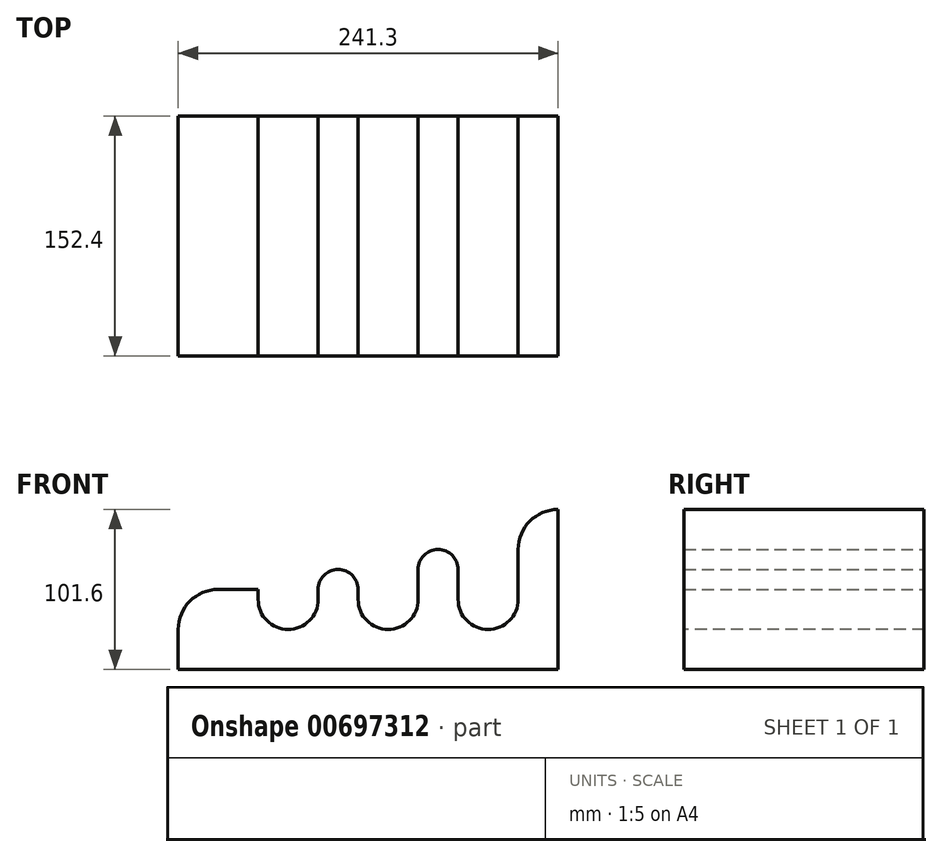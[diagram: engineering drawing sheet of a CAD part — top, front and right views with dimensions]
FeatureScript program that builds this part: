
annotation { "Feature Type Name" : "Feature", "Feature Type Description" : "" }
export const myFeature = defineFeature(function(context is Context, id is Id, definition is map)
    precondition{}
    {
        {
            var Q0;
            Q0=qCreatedBy(makeId("Front.planeOp"),FACE);
            var sketch = newSketch(context, id + "F0", { "sketchPlane" : qUnion([Q0])});
            skLineSegment(sketch, "E0.bottom", {"start": v(-172.92, 215.9) * mm, "end": v(-147.52, 215.9) * mm});
            skLineSegment(sketch, "E0.top", {"start": v(-172.92, 0) * mm, "end": v(-147.52, 0) * mm});
            skLineSegment(sketch, "E0.left", {"start": v(-172.92, 190.5) * mm, "end": v(-172.92, 152.4) * mm});
            skLineSegment(sketch, "E0.right", {"start": v(-147.52, 215.9) * mm, "end": v(-147.52, 0) * mm});
            skLineSegment(sketch, "E1.bottom", {"start": v(-147.52, 215.9) * mm, "end": v(-249.12, 215.9) * mm});
            skLineSegment(sketch, "E1.top", {"start": v(-172.92, 190.5) * mm, "end": v(-249.12, 190.5) * mm});
            skLineSegment(sketch, "E1.left", {"start": v(-147.52, 215.9) * mm, "end": v(-147.52, 190.5) * mm});
            skLineSegment(sketch, "E1.right", {"start": v(-249.12, 215.9) * mm, "end": v(-249.12, 190.5) * mm});
            skLineSegment(sketch, "E2.bottom", {"start": v(-172.92, 152.4) * mm, "end": v(-223.72, 152.4) * mm});
            skLineSegment(sketch, "E2.top", {"start": v(-172.92, 127) * mm, "end": v(-223.72, 127) * mm});
            skLineSegment(sketch, "E2.left", {"start": v(-147.52, 152.4) * mm, "end": v(-147.52, 127) * mm});
            skLineSegment(sketch, "E2.right", {"start": v(-223.72, 152.4) * mm, "end": v(-223.72, 127) * mm});
            skLineSegment(sketch, "E3.bottom", {"start": v(-172.92, 88.9) * mm, "end": v(-211.02, 88.9) * mm});
            skLineSegment(sketch, "E3.top", {"start": v(-172.92, 63.5) * mm, "end": v(-211.02, 63.5) * mm});
            skLineSegment(sketch, "E3.left", {"start": v(-147.52, 88.9) * mm, "end": v(-147.52, 63.5) * mm});
            skLineSegment(sketch, "E3.right", {"start": v(-211.02, 88.9) * mm, "end": v(-211.02, 63.5) * mm});
            skLineSegment(sketch, "E4.trimOffspring", {"start": v(-172.92, 63.5) * mm, "end": v(-172.92, 0) * mm});
            skLineSegment(sketch, "E5.trimOffspring", {"start": v(-172.92, 127) * mm, "end": v(-172.92, 88.9) * mm});
            skLineSegment(sketch, "E6.left", {"start": v(-172.92, 0) * mm, "end": v(-172.92, 25.4) * mm});
            skLineSegment(sketch, "E7.bottom", {"start": v(-172.92, 0) * mm, "end": v(-198.32, 0) * mm});
            skLineSegment(sketch, "E7.top", {"start": v(-172.92, 25.4) * mm, "end": v(-198.32, 25.4) * mm});
            skLineSegment(sketch, "E7.right", {"start": v(-198.32, 0) * mm, "end": v(-198.32, 25.4) * mm});
            skPoint(sketch, "E8.oppositeSnap0", {"position": v(-160.22, 0) * mm});
            skLineSegment(sketch, "E8.bottom", {"start": v(-147.52, 0) * mm, "end": v(-160.22, 0) * mm});
            skLineSegment(sketch, "E8.top", {"start": v(-147.52, -25.4) * mm, "end": v(-160.22, -25.4) * mm});
            skLineSegment(sketch, "E8.left", {"start": v(-147.52, 0) * mm, "end": v(-147.52, -25.4) * mm});
            skLineSegment(sketch, "E8.right", {"start": v(-160.22, 0) * mm, "end": v(-160.22, -25.4) * mm});
            skSolve(sketch);
        }
        {
            var Q0;
            Q0=qSketchRegion(id+"F0",true);
            extrude(context, id + "F1", {"entities" : qUnion([Q0]), "depth" : 152.4 * mm, "offsetDistance" : 25.4 * mm});
        }
        {
            var Q0;
            Q0=makeQuery(id+"F1.opExtrude","SWEPT_FACE",FACE,{"disambiguationData":[OSD([sQuery(id+"F0.wireOp",EDGE,"E8.right")])]});
            var sketch = newSketch(context, id + "F2", { "sketchPlane" : qUnion([Q0])});
            skLineSegment(sketch, "E9.bottom", {"start": v(0, 0) * mm, "end": v(152.4, 0) * mm});
            skLineSegment(sketch, "E9.top", {"start": v(0, -25.4) * mm, "end": v(152.4, -25.4) * mm});
            skLineSegment(sketch, "E9.left", {"start": v(0, 0) * mm, "end": v(0, -25.4) * mm});
            skLineSegment(sketch, "E9.right", {"start": v(152.4, 0) * mm, "end": v(152.4, -25.4) * mm});
            skSolve(sketch);
        }
        {
            var Q0;
            Q0=qSketchRegion(id+"F2",true);
            extrude(context, id + "F3", {"entities" : qUnion([Q0]), "operationType" : NewBodyOperationType.ADD, "depth" : 38.1 * mm, "offsetDistance" : 25.4 * mm});
        }
        {
            var Q0;
            Q0=makeQuery(id+"F3.opExtrude","CAP_EDGE",EDGE,{"disambiguationData":[OSD([sQuery(id+"F2.wireOp",EDGE,"E9.top")])],"isStart":false});
            fillet(context, id + "F4", {"entities" : qUnion([Q0]), "radius" : 25.4 * mm, "tangentPropagation" : true, "allowEdgeOverflow" : false});
        }
        {
            var Q0;
            Q0=makeQuery(id+"F3.boolean.opBoolean","MERGE",FACE,{"derivedFrom":[makeQuery(id+"F1.opExtrude","CAP_FACE",FACE,{"disambiguationData":[OSD([sQuery(id+"F0.wireOp",EDGE,"E0.top"),sQuery(id+"F0.wireOp",EDGE,"E0.left"),sQuery(id+"F0.wireOp",EDGE,"E0.right"),sQuery(id+"F0.wireOp",EDGE,"E1.bottom"),sQuery(id+"F0.wireOp",EDGE,"E1.top"),sQuery(id+"F0.wireOp",EDGE,"E1.left"),sQuery(id+"F0.wireOp",EDGE,"E1.right"),sQuery(id+"F0.wireOp",EDGE,"E2.bottom"),sQuery(id+"F0.wireOp",EDGE,"E2.top"),sQuery(id+"F0.wireOp",EDGE,"E2.left"),sQuery(id+"F0.wireOp",EDGE,"E2.right"),sQuery(id+"F0.wireOp",EDGE,"E3.bottom"),sQuery(id+"F0.wireOp",EDGE,"E3.top"),sQuery(id+"F0.wireOp",EDGE,"E3.left"),sQuery(id+"F0.wireOp",EDGE,"E3.right"),sQuery(id+"F0.wireOp",EDGE,"E4.trimOffspring"),sQuery(id+"F0.wireOp",EDGE,"E5.trimOffspring"),sQuery(id+"F0.wireOp",EDGE,"E7.bottom"),sQuery(id+"F0.wireOp",EDGE,"E7.top"),sQuery(id+"F0.wireOp",EDGE,"E7.right"),sQuery(id+"F0.wireOp",EDGE,"E8.top"),sQuery(id+"F0.wireOp",EDGE,"E8.left"),sQuery(id+"F0.wireOp",EDGE,"E8.right")])],"isStart":false}),makeQuery(id+"F3.opExtrude","SWEPT_FACE",FACE,{"disambiguationData":[OSD([sQuery(id+"F2.wireOp",EDGE,"E9.right")])]})]});
            var sketch = newSketch(context, id + "F5", { "sketchPlane" : qUnion([Q0])});
            skLineSegment(sketch, "E10.bottom", {"start": v(-249.12, 215.9) * mm, "end": v(-147.52, 215.9) * mm});
            skLineSegment(sketch, "E10.top", {"start": v(-211.02, 254) * mm, "end": v(-147.52, 254) * mm});
            skLineSegment(sketch, "E10.left", {"start": v(-249.12, 215.9) * mm, "end": v(-249.12, 215.9) * mm});
            skLineSegment(sketch, "E10.right", {"start": v(-147.52, 215.9) * mm, "end": v(-147.52, 254) * mm});
            skPoint(sketch, "E11.visualSharp", {"position": v(-249.12, 254) * mm});
            skArc(sketch, "E11.filletArc", {"start": v(-211.02, 254) * mm, "mid": v(-237.96, 242.84) * mm, "end": v(-249.12, 215.9) * mm});
            skSolve(sketch);
        }
        {
            var Q0;
            Q0=makeQuery(id+"F5.imprint","IMPRINT",FACE,{"disambiguationData":[TD([[makeQuery(id+"F5.imprint","IMPRINT",EDGE,{"derivedFrom":sQuery(id+"F5.wireOp",EDGE,"E10.bottom")}),-1.0]])]});
            extrude(context, id + "F6", {"entities" : qUnion([Q0]), "operationType" : NewBodyOperationType.ADD, "oppositeDirection" : true, "depth" : 151.9 * mm, "offsetDistance" : 25.4 * mm});
        }
        {
            var Q0;
            Q0=makeQuery(id+"F1.opExtrude","SWEPT_EDGE",EDGE,{"disambiguationData":[OSD([sQuery(id+"F0.wireOp",EDGE,"E3.bottom"),sQuery(id+"F0.wireOp",EDGE,"E5.trimOffspring")])]});
            fillet(context, id + "F7", {"entities" : qUnion([Q0]), "radius" : 19.05 * mm, "tangentPropagation" : true, "allowEdgeOverflow" : false});
        }
        {
            var Q0;
            Q0=makeQuery(id+"F1.opExtrude","SWEPT_EDGE",EDGE,{"disambiguationData":[OSD([sQuery(id+"F0.wireOp",EDGE,"E0.left"),sQuery(id+"F0.wireOp",EDGE,"E1.top")])]});
            var Q1;
            Q1=makeQuery(id+"F1.opExtrude","SWEPT_EDGE",EDGE,{"disambiguationData":[OSD([sQuery(id+"F0.wireOp",EDGE,"E2.top"),sQuery(id+"F0.wireOp",EDGE,"E5.trimOffspring")])]});
            fillet(context, id + "F8", {"entities" : qUnion([Q0, Q1]), "radius" : 19.05 * mm, "tangentPropagation" : true, "allowEdgeOverflow" : false});
        }
        {
            var Q0;
            Q0=makeQuery(id+"F1.opExtrude","SWEPT_EDGE",EDGE,{"disambiguationData":[OSD([sQuery(id+"F0.wireOp",EDGE,"E0.left"),sQuery(id+"F0.wireOp",EDGE,"E2.bottom")])]});
            var Q1;
            Q1=makeQuery(id+"F1.opExtrude","SWEPT_EDGE",EDGE,{"disambiguationData":[OSD([sQuery(id+"F0.wireOp",EDGE,"E4.trimOffspring"),sQuery(id+"F0.wireOp",EDGE,"E7.top"),sQuery(id+"F0.wireOp",EDGE,"E6.left")])]});
            var Q2;
            Q2=makeQuery(id+"F1.opExtrude","SWEPT_EDGE",EDGE,{"disambiguationData":[OSD([sQuery(id+"F0.wireOp",EDGE,"E3.top"),sQuery(id+"F0.wireOp",EDGE,"E4.trimOffspring")])]});
            fillet(context, id + "F9", {"entities" : qUnion([Q0, Q1, Q2]), "radius" : 19.05 * mm, "tangentPropagation" : true, "allowEdgeOverflow" : false});
        }
        {
            var Q0;
            Q0=makeQuery(id+"F1.opExtrude","SWEPT_EDGE",EDGE,{"disambiguationData":[OSD([sQuery(id+"F0.wireOp",EDGE,"E2.bottom"),sQuery(id+"F0.wireOp",EDGE,"E2.right")])]});
            var Q1;
            Q1=makeQuery(id+"F1.opExtrude","SWEPT_EDGE",EDGE,{"disambiguationData":[OSD([sQuery(id+"F0.wireOp",EDGE,"E2.top"),sQuery(id+"F0.wireOp",EDGE,"E2.right")])]});
            var Q2;
            Q2=makeQuery(id+"F1.opExtrude","SWEPT_EDGE",EDGE,{"disambiguationData":[OSD([sQuery(id+"F0.wireOp",EDGE,"E3.bottom"),sQuery(id+"F0.wireOp",EDGE,"E3.right")])]});
            var Q3;
            Q3=makeQuery(id+"F1.opExtrude","SWEPT_EDGE",EDGE,{"disambiguationData":[OSD([sQuery(id+"F0.wireOp",EDGE,"E3.top"),sQuery(id+"F0.wireOp",EDGE,"E3.right")])]});
            fillet(context, id + "F10", {"entities" : qUnion([Q0, Q1, Q2, Q3]), "radius" : 12.7 * mm, "tangentPropagation" : true, "allowEdgeOverflow" : false});
        }
        {
            var Q0;
            Q0=makeQuery(id+"F1.opExtrude","SWEPT_EDGE",EDGE,{"disambiguationData":[OSD([sQuery(id+"F0.wireOp",EDGE,"E1.top"),sQuery(id+"F0.wireOp",EDGE,"E1.right")])]});
            fillet(context, id + "F11", {"entities" : qUnion([Q0]), "radius" : 25.4 * mm, "tangentPropagation" : true, "allowEdgeOverflow" : false});
        }
        {
            var Q0;
            Q0=makeQuery(id+"F1.opExtrude","SWEPT_BODY",BODY,{"disambiguationData":[OSD([sQuery(id+"F0.wireOp",EDGE,"E0.top"),sQuery(id+"F0.wireOp",EDGE,"E0.left"),sQuery(id+"F0.wireOp",EDGE,"E0.right"),sQuery(id+"F0.wireOp",EDGE,"E1.bottom"),sQuery(id+"F0.wireOp",EDGE,"E1.top"),sQuery(id+"F0.wireOp",EDGE,"E1.left"),sQuery(id+"F0.wireOp",EDGE,"E1.right"),sQuery(id+"F0.wireOp",EDGE,"E2.bottom"),sQuery(id+"F0.wireOp",EDGE,"E2.top"),sQuery(id+"F0.wireOp",EDGE,"E2.left"),sQuery(id+"F0.wireOp",EDGE,"E2.right"),sQuery(id+"F0.wireOp",EDGE,"E3.bottom"),sQuery(id+"F0.wireOp",EDGE,"E3.top"),sQuery(id+"F0.wireOp",EDGE,"E3.left"),sQuery(id+"F0.wireOp",EDGE,"E3.right"),sQuery(id+"F0.wireOp",EDGE,"E4.trimOffspring"),sQuery(id+"F0.wireOp",EDGE,"E5.trimOffspring"),sQuery(id+"F0.wireOp",EDGE,"E7.bottom"),sQuery(id+"F0.wireOp",EDGE,"E7.top"),sQuery(id+"F0.wireOp",EDGE,"E7.right"),sQuery(id+"F0.wireOp",EDGE,"E8.top"),sQuery(id+"F0.wireOp",EDGE,"E8.left"),sQuery(id+"F0.wireOp",EDGE,"E8.right")])]});
            var Q1;
            Q1=makeQuery(id+"F1.opExtrude","SWEPT_EDGE",EDGE,{"disambiguationData":[OSD([sQuery(id+"F0.wireOp",EDGE,"E8.top"),sQuery(id+"F0.wireOp",EDGE,"E8.left")])]});
            transform(context, id + "F12", {"entities" : qUnion([Q0]), "transformType" : TransformType.ROTATION, "transformAxis" : qUnion([Q1]), "angle" : 90 * degree, "makeCopy" : false});
        }
    });
